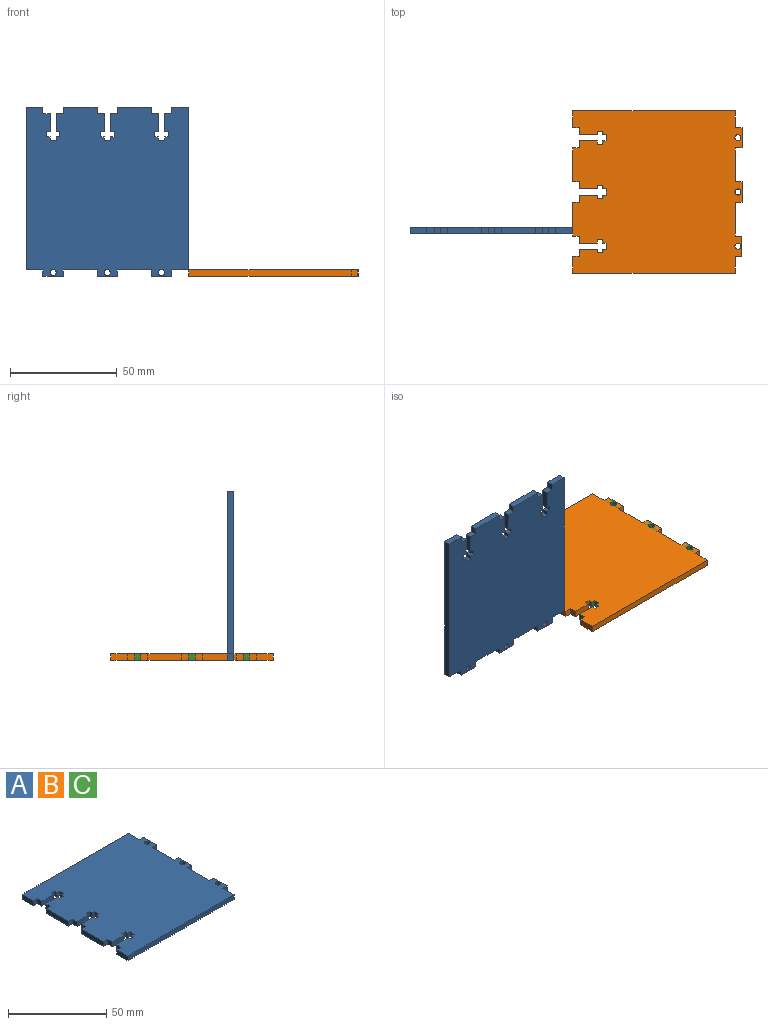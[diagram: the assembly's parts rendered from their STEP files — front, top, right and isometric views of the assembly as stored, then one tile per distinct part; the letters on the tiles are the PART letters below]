
ASSEMBLY  parts=3 mates=1
PART A: 69 faces, bbox 79.3x76.2x3 mm
  f0: plane 2.97x1.75mm, normal (1,0,0), area 5.2mm2, adj f1,f65,f67,f68
  f1: plane 2.97x2.38mm, normal (0,-1,0), area 7.1mm2, adj f0,f2,f67,f68
  f2: plane 2.97x1.75mm, normal (-1,0,0), area 5.2mm2, adj f1,f3,f67,f68
  f3: plane 2.97x1.85mm, normal (0,-1,0), area 5.5mm2, adj f2,f4,f67,f68
  f4: plane 2.97x2.85mm, normal (-1,0,0), area 8.5mm2, adj f3,f5,f67,f68
  f5: plane 2.97x1.85mm, normal (0,1,0), area 5.5mm2, adj f4,f6,f67,f68
  f6: plane 2.97x1.75mm, normal (-1,0,0), area 5.2mm2, adj f5,f7,f67,f68
  f7: plane 2.97x2.38mm, normal (0,1,0), area 7.1mm2, adj f6,f8,f67,f68
  f8: plane 2.97x1.75mm, normal (1,0,0), area 5.2mm2, adj f7,f9,f67,f68
  f9: plane 8.47x2.97mm, normal (0,1,0), area 25.2mm2, adj f8,f10,f67,f68
  f10: plane 3.34x2.97mm, normal (-1,0,0), area 9.9mm2, adj f9,f11,f67,f68
  f11: plane 2.97x2.97mm, normal (0,1,0), area 8.8mm2, adj f10,f12,f67,f68
  f12: plane 15.88x2.97mm, normal (-1,0,0), area 47.2mm2, adj f11,f13,f67,f68
  f13: plane 2.97x2.97mm, normal (0,-1,0), area 8.8mm2, adj f12,f14,f67,f68
  f14: plane 3.34x2.97mm, normal (-1,0,0), area 9.9mm2, adj f13,f15,f67,f68
  f15: plane 8.47x2.97mm, normal (0,-1,0), area 25.2mm2, adj f14,f16,f67,f68
  f16: plane 2.97x1.75mm, normal (1,0,0), area 5.2mm2, adj f15,f17,f67,f68
  f17: plane 2.97x2.38mm, normal (0,-1,0), area 7.1mm2, adj f16,f18,f67,f68
  f18: plane 2.97x1.75mm, normal (-1,0,0), area 5.2mm2, adj f17,f19,f67,f68
  f19: plane 2.97x1.85mm, normal (0,-1,0), area 5.5mm2, adj f18,f20,f67,f68
  f20: plane 2.97x2.85mm, normal (-1,0,0), area 8.5mm2, adj f19,f21,f67,f68
  f21: plane 2.97x1.85mm, normal (0,1,0), area 5.5mm2, adj f20,f22,f67,f68
  f22: plane 2.97x1.75mm, normal (-1,0,0), area 5.2mm2, adj f21,f23,f67,f68
  f23: plane 2.97x2.38mm, normal (0,1,0), area 7.1mm2, adj f22,f24,f67,f68
  f24: plane 2.97x1.75mm, normal (1,0,0), area 5.2mm2, adj f23,f25,f67,f68
  f25: plane 8.47x2.97mm, normal (0,1,0), area 25.2mm2, adj f24,f26,f67,f68
  f26: plane 3.34x2.97mm, normal (-1,0,0), area 9.9mm2, adj f25,f27,f67,f68
  f27: plane 2.97x2.97mm, normal (0,1,0), area 8.8mm2, adj f26,f28,f67,f68
  f28: plane 15.88x2.97mm, normal (-1,0,0), area 47.2mm2, adj f27,f29,f67,f68
  f29: plane 2.97x2.97mm, normal (0,-1,0), area 8.8mm2, adj f28,f30,f67,f68
  f30: plane 3.34x2.97mm, normal (-1,0,0), area 9.9mm2, adj f29,f31,f67,f68
  f31: plane 8.47x2.97mm, normal (0,-1,0), area 25.2mm2, adj f30,f32,f67,f68
  f32: plane 2.97x1.75mm, normal (1,0,0), area 5.2mm2, adj f31,f33,f67,f68
  f33: plane 2.97x2.38mm, normal (0,-1,0), area 7.1mm2, adj f32,f34,f67,f68
  f34: plane 2.97x1.75mm, normal (-1,0,0), area 5.2mm2, adj f33,f35,f67,f68
  f35: plane 2.97x1.85mm, normal (0,-1,0), area 5.5mm2, adj f34,f36,f67,f68
  f36: plane 2.97x2.84mm, normal (-1,0,0), area 8.5mm2, adj f35,f37,f67,f68
  f37: plane 2.97x1.85mm, normal (0,1,0), area 5.5mm2, adj f36,f38,f67,f68
  f38: plane 2.97x1.75mm, normal (-1,0,0), area 5.2mm2, adj f37,f39,f67,f68
  f39: plane 2.97x2.38mm, normal (0,1,0), area 7.1mm2, adj f38,f40,f67,f68
  f40: plane 2.97x1.75mm, normal (1,0,0), area 5.2mm2, adj f39,f41,f67,f68
  f41: plane 8.47x2.97mm, normal (0,1,0), area 25.2mm2, adj f40,f42,f67,f68
  f42: plane 3.34x2.97mm, normal (-1,0,0), area 9.9mm2, adj f41,f43,f67,f68
  f43: plane 2.97x2.97mm, normal (0,1,0), area 8.8mm2, adj f42,f44,f67,f68
  f44: plane 7.94x2.97mm, normal (-1,0,0), area 23.6mm2, adj f43,f45,f67,f68
  f45: plane 76.2x2.97mm, normal (0,-1,0), area 226.5mm2, adj f44,f46,f67,f68
  f46: plane 7.94x2.97mm, normal (1,0,0), area 23.6mm2, adj f45,f47,f67,f68
  f47: plane 2.97x2.97mm, normal (0,-1,0), area 8.8mm2, adj f46,f48,f67,f68
  f48: plane 9.53x2.97mm, normal (1,0,0), area 28.3mm2, adj f47,f49,f67,f68
  f49: plane 2.97x2.97mm, normal (0,1,0), area 8.8mm2, adj f48,f50,f67,f68
  f50: plane 15.88x2.97mm, normal (1,0,0), area 47.2mm2, adj f49,f51,f67,f68
  f51: plane 3.1x2.97mm, normal (0,-1,0), area 9.2mm2, adj f50,f52,f67,f68
  f52: plane 9.53x2.97mm, normal (1,0,0), area 28.3mm2, adj f51,f53,f67,f68
  f53: plane 3.1x2.97mm, normal (0,1,0), area 9.2mm2, adj f52,f54,f67,f68
  f54: plane 15.88x2.97mm, normal (1,0,0), area 47.2mm2, adj f53,f55,f67,f68
  f55: plane 3.1x2.97mm, normal (0,-1,0), area 9.2mm2, adj f54,f56,f67,f68
  f56: plane 9.53x2.97mm, normal (1,0,0), area 28.3mm2, adj f55,f57,f67,f68
  f57: plane 3.1x2.97mm, normal (0,1,0), area 9.2mm2, adj f56,f58,f67,f68
  f58: plane 7.94x2.97mm, normal (1,0,0), area 23.6mm2, adj f57,f59,f67,f68
  f59: plane 76.2x2.97mm, normal (0,1,0), area 226.5mm2, adj f58,f60,f67,f68
  f60: plane 7.94x2.97mm, normal (-1,0,0), area 23.6mm2, adj f59,f61,f67,f68
  f61: plane 2.97x2.97mm, normal (0,-1,0), area 8.8mm2, adj f60,f62,f67,f68
  f62: plane 3.34x2.97mm, normal (-1,0,0), area 9.9mm2, adj f61,f65,f67,f68
  f63: cylinder r=1.42mm len=2.97mm, axis (0,0,-1), area 26.6mm2, adj f67,f68
  f64: cylinder r=1.42mm len=2.97mm, axis (0,0,-1), area 26.6mm2, adj f67,f68
  f65: plane 8.47x2.97mm, normal (0,-1,0), area 25.2mm2, adj f0,f62,f67,f68
  f66: cylinder r=1.42mm len=2.97mm, axis (0,0,-1), area 26.6mm2, adj f67,f68
  f67: plane 79.3x76.2mm, normal (0,0,1), area 5656.4mm2, adj f0,f1,f2,f3,f4,f5,f6,f7
  f68: plane 79.3x76.2mm, normal (0,0,-1), area 5656.4mm2, adj f0,f1,f2,f3,f4,f5,f6,f7
PART B: same geometry as A
PART C: same geometry as A
PLACE A rot(axis=(0.58,0.58,-0.58),120deg) t=(-97.97,26.26,88.39)mm
PLACE B t=(-21.69,4.75,9.27)mm fixed
PLACE C t=(-21.69,4.75,9.27)mm
MATE parallel B.f67 <-> A.f48  axis (0,0,1) through (18.1,42.86,12.25)mm
